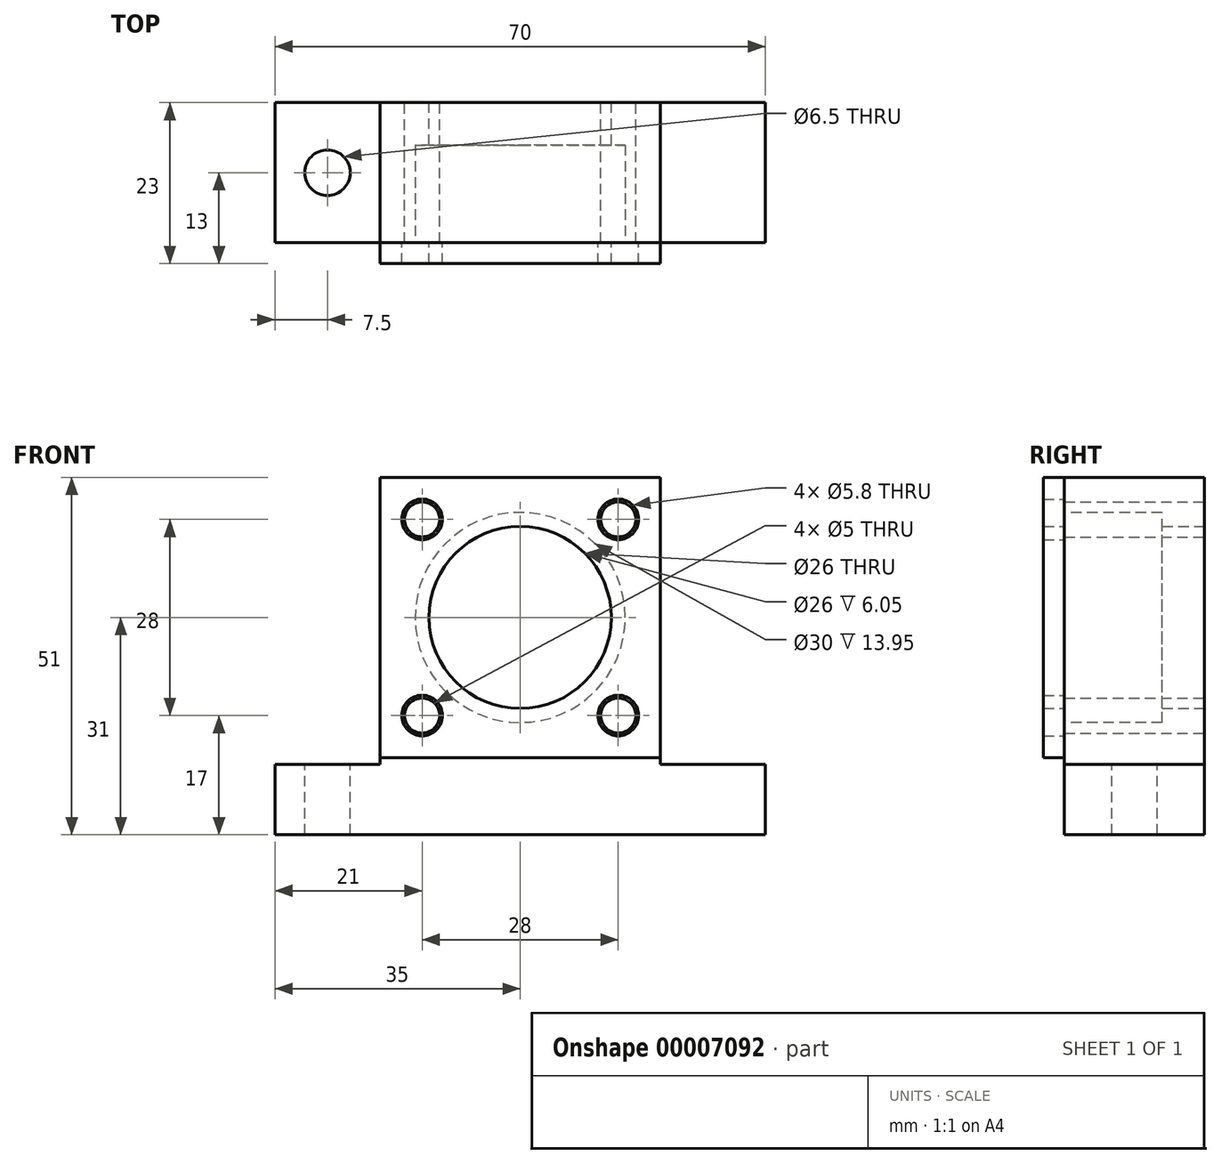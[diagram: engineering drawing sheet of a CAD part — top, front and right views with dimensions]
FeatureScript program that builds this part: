
annotation { "Feature Type Name" : "Feature", "Feature Type Description" : "" }
export const myFeature = defineFeature(function(context is Context, id is Id, definition is map)
    precondition{}
    {
        {
            var Q0;
            Q0=qCreatedBy(makeId("Front.planeOp"),FACE);
            var sketch = newSketch(context, id + "F0", { "sketchPlane" : qUnion([Q0])});
            skLineSegment(sketch, "E0.rect.bottom", {"start": v(20, -21) * mm, "end": v(-20, -21) * mm});
            skLineSegment(sketch, "E0.rect.top", {"start": v(20, 20) * mm, "end": v(-20, 20) * mm});
            skLineSegment(sketch, "E0.rect.left", {"start": v(20, -21) * mm, "end": v(20, 20) * mm});
            skLineSegment(sketch, "E0.rect.right", {"start": v(-20, -21) * mm, "end": v(-20, 20) * mm});
            skPoint(sketch, "E0.rect.middle", {"position": v(0, -0.5) * mm});
            skLineSegment(sketch, "E1.bottom", {"start": v(-35, -21) * mm, "end": v(35, -21) * mm});
            skLineSegment(sketch, "E1.top", {"start": v(-35, -31) * mm, "end": v(35, -31) * mm});
            skLineSegment(sketch, "E1.left", {"start": v(-35, -21) * mm, "end": v(-35, -31) * mm});
            skLineSegment(sketch, "E1.right", {"start": v(35, -21) * mm, "end": v(35, -31) * mm});
            skCircle(sketch, "E2", {"center": v(-14, 14) * mm, "radius": 2.5 * mm});
            skCircle(sketch, "E3.0.MirrorC", {"center": v(14, 14) * mm, "radius": 2.5 * mm});
            skCircle(sketch, "E4.0.MirrorC", {"center": v(14, -14) * mm, "radius": 2.5 * mm});
            skCircle(sketch, "E5.0.MirrorC", {"center": v(-14, -14) * mm, "radius": 2.5 * mm});
            skCircle(sketch, "E6", {"center": v(0, 0) * mm, "radius": 13 * mm});
            skSolve(sketch);
        }
        {
            var Q0;
            Q0=makeQuery(id+"F0.imprint","IMPRINT",FACE,{"disambiguationData":[TD([[makeQuery(id+"F0.imprint","IMPRINT",EDGE,{"derivedFrom":sQuery(id+"F0.wireOp",EDGE,"E0.rect.top")}),1.0]])]});
            var Q1;
            Q1=makeQuery(id+"F0.imprint","IMPRINT",FACE,{"disambiguationData":[TD([[makeQuery(id+"F0.imprint","IMPRINT",EDGE,{"derivedFrom":sQuery(id+"F0.wireOp",EDGE,"E1.top")}),1.0]])]});
            extrude(context, id + "F1", {"entities" : qUnion([Q0, Q1]), "depth" : 20 * mm});
        }
        {
            var Q0;
            Q0=makeQuery(id+"F1.opExtrude","CAP_FACE",FACE,{"disambiguationData":[OSD([sQuery(id+"F0.wireOp",EDGE,"E0.rect.top"),sQuery(id+"F0.wireOp",EDGE,"E0.rect.left"),sQuery(id+"F0.wireOp",EDGE,"E0.rect.right"),sQuery(id+"F0.wireOp",EDGE,"E1.bottom"),sQuery(id+"F0.wireOp",EDGE,"E1.top"),sQuery(id+"F0.wireOp",EDGE,"E1.left"),sQuery(id+"F0.wireOp",EDGE,"E1.right"),sQuery(id+"F0.wireOp",EDGE,"E2"),sQuery(id+"F0.wireOp",EDGE,"E3.0.MirrorC"),sQuery(id+"F0.wireOp",EDGE,"E4.0.MirrorC"),sQuery(id+"F0.wireOp",EDGE,"E5.0.MirrorC"),sQuery(id+"F0.wireOp",EDGE,"E6")])],"isStart":false});
            var sketch = newSketch(context, id + "F2", { "sketchPlane" : qUnion([Q0])});
            skCircle(sketch, "E7", {"center": v(0, 0) * mm, "radius": 15 * mm});
            skSolve(sketch);
        }
        {
            var Q0;
            Q0=makeQuery(id+"F2.imprint","IMPRINT",FACE,{"disambiguationData":[TD([[makeQuery(id+"F2.imprint","IMPRINT",EDGE,{"derivedFrom":sQuery(id+"F2.wireOp",EDGE,"E7")}),1.0]])]});
            extrude(context, id + "F3", {"entities" : qUnion([Q0]), "operationType" : NewBodyOperationType.REMOVE, "oppositeDirection" : true, "depth" : 13.95 * mm});
        }
        {
            var Q0;
            {var subQ0=sQuery(id+"F0.wireOp",EDGE,"E1.bottom");Q0=makeQuery(id+"F1.opExtrude","SWEPT_FACE",FACE,{"disambiguationData":[OSD([subQ0]),TDD([makeQuery(id+"F0.imprint","IMPRINT",EDGE,{"disambiguationData":[TD([[makeQuery(id+"F0.imprint","INTERSECT",VERTEX,{"derivedFrom":[sQuery(id+"F0.wireOp",EDGE,"E0.rect.right"),subQ0]}),1.0]])],"derivedFrom":subQ0})])]});}
            var sketch = newSketch(context, id + "F4", { "sketchPlane" : qUnion([Q0])});
            skCircle(sketch, "E8", {"center": v(-27.5, -10) * mm, "radius": 3.25 * mm});
            skLineSegment(sketch, "E9", {"start": v(-35, -10) * mm, "end": v(-20, -10) * mm, "construction": true});
            skCircle(sketch, "E10.0.MirrorC", {"center": v(27.5, -10) * mm, "radius": 3.25 * mm});
            skSolve(sketch);
        }
        {
            var Q0;
            Q0=makeQuery(id+"F4.imprint","IMPRINT",FACE,{"disambiguationData":[TD([[makeQuery(id+"F4.imprint","IMPRINT",EDGE,{"derivedFrom":sQuery(id+"F4.wireOp",EDGE,"E8")}),1.0]])]});
            var Q1;
            Q1=makeQuery(id+"F4.imprint","IMPRINT",FACE,{"disambiguationData":[TD([[makeQuery(id+"F4.imprint","IMPRINT",EDGE,{"derivedFrom":sQuery(id+"F4.wireOp",EDGE,"E10.0.MirrorC")}),-1.0]])]});
            extrude(context, id + "F5", {"entities" : qUnion([Q0, Q1]), "operationType" : NewBodyOperationType.REMOVE, "endBound" : BoundingType.THROUGH_ALL, "oppositeDirection" : true, "depth" : 25 * mm});
        }
        {
            var Q0;
            Q0=makeQuery(id+"F1.opExtrude","CAP_FACE",FACE,{"disambiguationData":[OSD([sQuery(id+"F0.wireOp",EDGE,"E0.rect.top"),sQuery(id+"F0.wireOp",EDGE,"E0.rect.left"),sQuery(id+"F0.wireOp",EDGE,"E0.rect.right"),sQuery(id+"F0.wireOp",EDGE,"E1.bottom"),sQuery(id+"F0.wireOp",EDGE,"E1.top"),sQuery(id+"F0.wireOp",EDGE,"E1.left"),sQuery(id+"F0.wireOp",EDGE,"E1.right"),sQuery(id+"F0.wireOp",EDGE,"E2"),sQuery(id+"F0.wireOp",EDGE,"E3.0.MirrorC"),sQuery(id+"F0.wireOp",EDGE,"E4.0.MirrorC"),sQuery(id+"F0.wireOp",EDGE,"E5.0.MirrorC"),sQuery(id+"F0.wireOp",EDGE,"E6")])],"isStart":false});
            var sketch = newSketch(context, id + "F6", { "sketchPlane" : qUnion([Q0])});
            skLineSegment(sketch, "E11.bottom", {"start": v(-20, 20) * mm, "end": v(20, 20) * mm});
            skLineSegment(sketch, "E11.top", {"start": v(-20, -20) * mm, "end": v(20, -20) * mm});
            skLineSegment(sketch, "E11.left", {"start": v(-20, 20) * mm, "end": v(-20, -20) * mm});
            skLineSegment(sketch, "E11.right", {"start": v(20, 20) * mm, "end": v(20, -20) * mm});
            skCircle(sketch, "E12.0", {"center": v(0, 0) * mm, "radius": 13 * mm});
            skCircle(sketch, "E13", {"center": v(-14, 14) * mm, "radius": 2.9 * mm});
            skCircle(sketch, "E14", {"center": v(14, 14) * mm, "radius": 2.9 * mm});
            skCircle(sketch, "E15", {"center": v(14, -14) * mm, "radius": 2.9 * mm});
            skCircle(sketch, "E16", {"center": v(-14, -14) * mm, "radius": 2.9 * mm});
            skSolve(sketch);
        }
        {
            var Q0;
            Q0=makeQuery(id+"F6.imprint","IMPRINT",FACE,{"disambiguationData":[TD([[makeQuery(id+"F6.imprint","IMPRINT",EDGE,{"derivedFrom":sQuery(id+"F6.wireOp",EDGE,"E11.bottom")}),1.0]])]});
            var Q1;
            Q1=makeQuery(id+"F6.imprint","IMPRINT",FACE,{"disambiguationData":[TD([[makeQuery(id+"F6.imprint","IMPRINT",EDGE,{"derivedFrom":sQuery(id+"F6.wireOp",EDGE,"E12.0")}),-1.0]])]});
            extrude(context, id + "F7", {"entities" : qUnion([Q0, Q1]), "depth" : 3 * mm});
        }
    });
